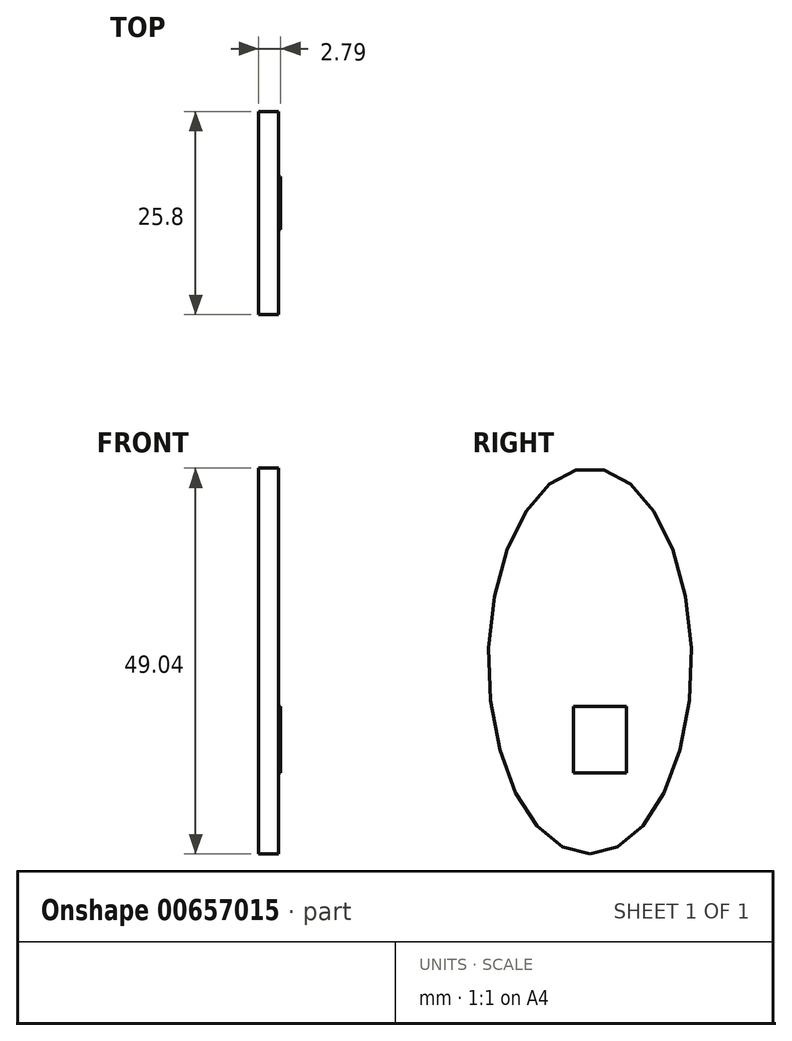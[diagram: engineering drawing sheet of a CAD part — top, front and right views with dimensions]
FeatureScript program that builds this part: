
annotation { "Feature Type Name" : "Feature", "Feature Type Description" : "" }
export const myFeature = defineFeature(function(context is Context, id is Id, definition is map)
    precondition{}
    {
        {
            var Q0;
            Q0=qCreatedBy(makeId("Right.planeOp"),FACE);
            var sketch = newSketch(context, id + "F0", { "sketchPlane" : qUnion([Q0])});
            skEllipse(sketch, "E0", {"center": v(-45.33, 52.75) * mm, "majorRadius": 24.52 * mm, "minorRadius": 12.9 * mm, "majorAxis": v(0, -1)});
            skSolve(sketch);
        }
        {
            var Q0;
            Q0 = qSketchRegion(id + "F0", true);
            extrude(context, id + "F1", {"entities" : qUnion([Q0]), "depth" : 2.54 * mm, "offsetDistance" : 25.4 * mm});
        }
        {
            var Q0;
            Q0=makeQuery(id+"F1.opExtrude","CAP_FACE",FACE,{"disambiguationData":[OSD([sQuery(id+"F0.wireOp",EDGE,"E0")])],"isStart":false});
            var sketch = newSketch(context, id + "F2", { "sketchPlane" : qUnion([Q0])});
            skLineSegment(sketch, "E1.bottom", {"start": v(-47.42, 46.97) * mm, "end": v(-40.7, 46.97) * mm});
            skLineSegment(sketch, "E1.top", {"start": v(-47.42, 38.55) * mm, "end": v(-40.7, 38.55) * mm});
            skLineSegment(sketch, "E1.left", {"start": v(-47.42, 46.97) * mm, "end": v(-47.42, 38.55) * mm});
            skLineSegment(sketch, "E1.right", {"start": v(-40.7, 46.97) * mm, "end": v(-40.7, 38.55) * mm});
            skSolve(sketch);
        }
        {
            var Q0;
            Q0 = qSketchRegion(id + "F2", true);
            extrude(context, id + "F3", {"entities" : qUnion([Q0]), "operationType" : NewBodyOperationType.ADD, "depth" : 0.25 * mm, "offsetDistance" : 25.4 * mm});
        }
    });
